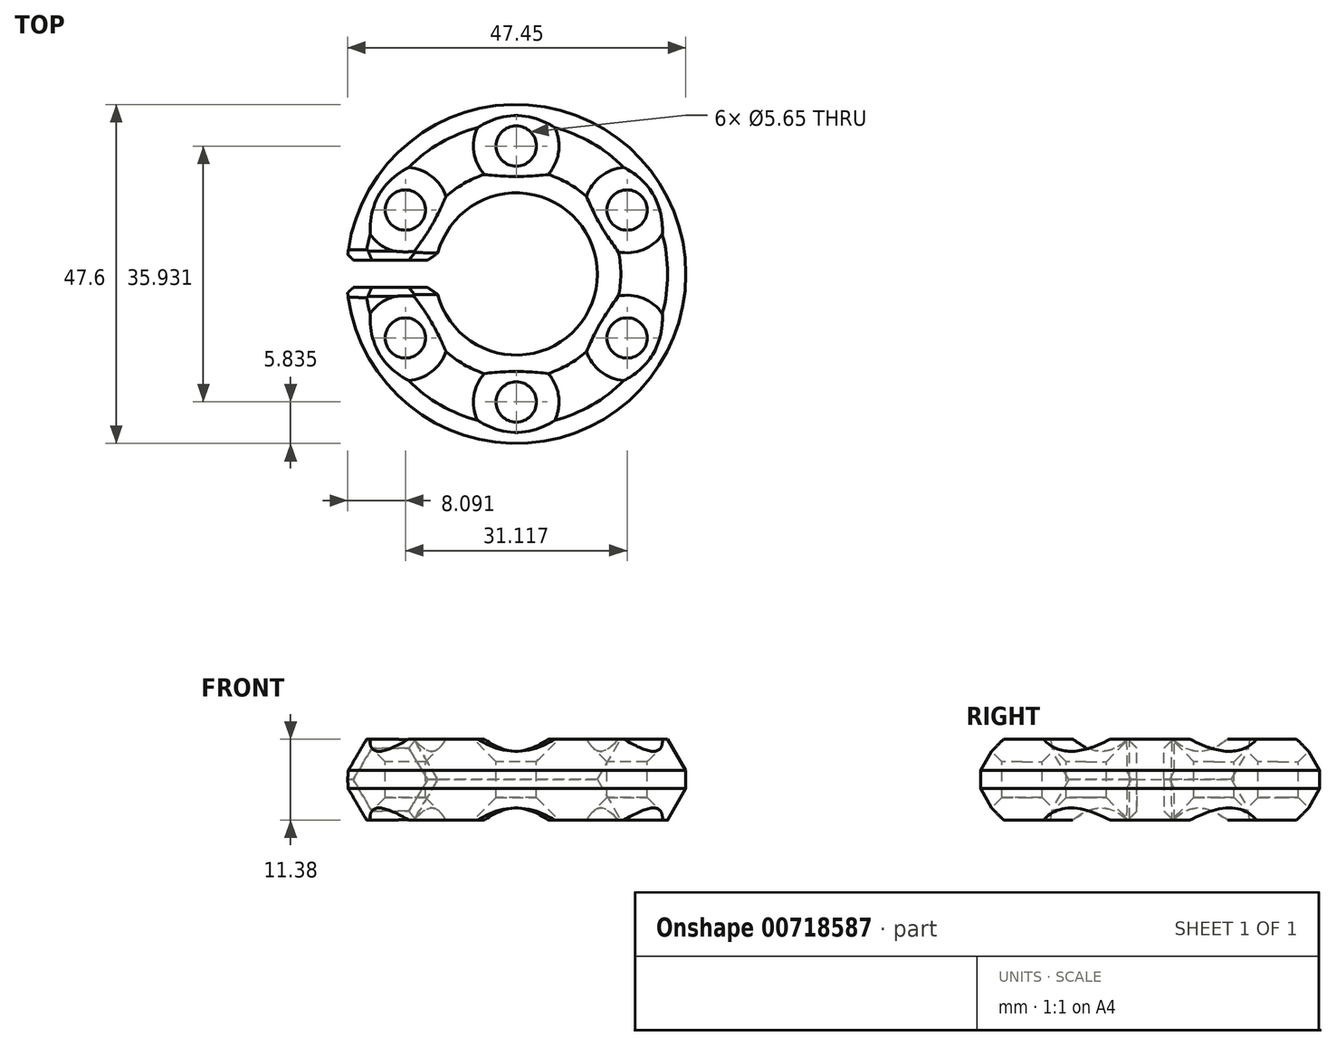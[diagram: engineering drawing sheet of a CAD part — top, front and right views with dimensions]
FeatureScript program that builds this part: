
annotation { "Feature Type Name" : "Feature", "Feature Type Description" : "" }
export const myFeature = defineFeature(function(context is Context, id is Id, definition is map)
    precondition{}
    {
        {
            var Q0;
            Q0=qCreatedBy(makeId("Front.planeOp"),FACE);
            var sketch = newSketch(context, id + "F0", { "sketchPlane" : qUnion([Q0])});
            skCircle(sketch, "E0.cCircle", {"center": v(-17.96, 0) * mm, "radius": 5.7 * mm, "construction": true});
            skLineSegment(sketch, "E0.0", {"start": v(-14.67, -5.7) * mm, "end": v(-21.25, -5.7) * mm});
            skLineSegment(sketch, "E0.1", {"start": v(-21.25, -5.7) * mm, "end": v(-24.53, 0) * mm});
            skLineSegment(sketch, "E0.2", {"start": v(-24.53, 0) * mm, "end": v(-21.25, 5.7) * mm});
            skLineSegment(sketch, "E0.3", {"start": v(-21.25, 5.7) * mm, "end": v(-14.67, 5.7) * mm});
            skLineSegment(sketch, "E0.4", {"start": v(-14.67, 5.7) * mm, "end": v(-11.38, 0) * mm});
            skLineSegment(sketch, "E0.5", {"start": v(-11.38, 0) * mm, "end": v(-14.67, -5.7) * mm});
            skPoint(sketch, "E0.0.midPoint", {"position": v(-17.96, -5.7) * mm});
            skLineSegment(sketch, "E1", {"start": v(0, 30.8) * mm, "end": v(0, -30.51) * mm});
            skSolve(sketch);
        }
        {
            var Q0;
            Q0 = qSketchRegion(id + "F0", true);
            var Q1;
            Q1=sQuery(id+"F0.wireOp",EDGE,"E1");
            revolve(context, id + "F1", {"surfaceOperationType" : NewSurfaceOperationType.NEW, "entities" : qUnion([Q0]), "axis" : qUnion([Q1]), "revolveType" : RevolveType.FULL});
        }
        {
            var Q0;
            Q0=qCreatedBy(makeId("Top.planeOp"),FACE);
            var sketch = newSketch(context, id + "F2", { "sketchPlane" : qUnion([Q0])});
            skLineSegment(sketch, "E2.bottom", {"start": v(-9.68, 1.96) * mm, "end": v(-30.83, 1.96) * mm});
            skLineSegment(sketch, "E2.top", {"start": v(-9.68, -1.87) * mm, "end": v(-30.83, -1.87) * mm});
            skLineSegment(sketch, "E2.left", {"start": v(-9.68, 1.96) * mm, "end": v(-9.68, -1.87) * mm});
            skLineSegment(sketch, "E2.right", {"start": v(-30.83, 1.96) * mm, "end": v(-30.83, -1.87) * mm});
            skSolve(sketch);
        }
        {
            var Q0;
            Q0=makeQuery(id+"F2.imprint","IMPRINT",FACE,{"disambiguationData":[TD([[makeQuery(id+"F2.imprint","IMPRINT",EDGE,{"derivedFrom":sQuery(id+"F2.wireOp",EDGE,"E2.bottom")}),1.0]])]});
            extrude(context, id + "F3", {"entities" : qUnion([Q0]), "operationType" : NewBodyOperationType.REMOVE, "endBound" : BoundingType.SYMMETRIC, "depth" : 18.08 * mm, "offsetDistance" : 25.4 * mm});
        }
        {
            var Q0;
            Q0=makeQuery(id+"F3.boolean.opBoolean","COPY",FACE,{"derivedFrom":makeQuery(id+"F3.opExtrude","SWEPT_FACE",FACE,{"disambiguationData":[OSD([sQuery(id+"F2.wireOp",EDGE,"E2.bottom")])]})});
            var Q1;
            Q1=makeQuery(id+"F3.boolean.opBoolean","COPY",FACE,{"derivedFrom":makeQuery(id+"F3.opExtrude","SWEPT_FACE",FACE,{"disambiguationData":[OSD([sQuery(id+"F2.wireOp",EDGE,"E2.top")])]})});
            chamfer(context, id + "F4", {"entities" : qUnion([Q0, Q1]), "width" : 1.27 * mm, "tangentPropagation" : true});
        }
        {
            var Q0;
            Q0=qCreatedBy(makeId("Top.planeOp"),FACE);
            var sketch = newSketch(context, id + "F5", { "sketchPlane" : qUnion([Q0])});
            skCircle(sketch, "E3", {"center": v(0, -17.97) * mm, "radius": 2.82 * mm});
            skCircle(sketch, "E4.1.0", {"center": v(-15.56, -8.98) * mm, "radius": 2.82 * mm});
            skCircle(sketch, "E4.2.0", {"center": v(-15.56, 8.98) * mm, "radius": 2.82 * mm});
            skCircle(sketch, "E4.3.0", {"center": v(0, 17.97) * mm, "radius": 2.82 * mm});
            skCircle(sketch, "E4.4.0", {"center": v(15.56, 8.98) * mm, "radius": 2.82 * mm});
            skCircle(sketch, "E4.5.0", {"center": v(15.56, -8.98) * mm, "radius": 2.82 * mm});
            skPoint(sketch, "E4.center", {"position": v(0, 0) * mm});
            skLineSegment(sketch, "E4.anchor1", {"start": v(0, 0) * mm, "end": v(0, -17.97) * mm, "construction": true});
            skLineSegment(sketch, "E4.anchor2", {"start": v(0, 0) * mm, "end": v(15.56, -8.98) * mm, "construction": true});
            skSolve(sketch);
        }
        {
            var Q0;
            Q0 = qSketchRegion(id + "F5", true);
            extrude(context, id + "F6", {"entities" : qUnion([Q0]), "operationType" : NewBodyOperationType.REMOVE, "endBound" : BoundingType.SYMMETRIC, "oppositeDirection" : true, "depth" : 25.4 * mm, "offsetDistance" : 25.4 * mm});
        }
        {
            var Q0;
            Q0=makeQuery(id+"F6.boolean.opBoolean","INTERSECT",EDGE,{"derivedFrom":[makeQuery(id+"F1.opRevolve","SWEPT_FACE",FACE,{"disambiguationData":[OSD([sQuery(id+"F0.wireOp",EDGE,"E0.0")])]}),makeQuery(id+"F6.opExtrude","SWEPT_FACE",FACE,{"disambiguationData":[OSD([sQuery(id+"F5.wireOp",EDGE,"E4.1.0")])]})]});
            var Q1;
            Q1=makeQuery(id+"F6.boolean.opBoolean","INTERSECT",EDGE,{"derivedFrom":[makeQuery(id+"F1.opRevolve","SWEPT_FACE",FACE,{"disambiguationData":[OSD([sQuery(id+"F0.wireOp",EDGE,"E0.0")])]}),makeQuery(id+"F6.opExtrude","SWEPT_FACE",FACE,{"disambiguationData":[OSD([sQuery(id+"F5.wireOp",EDGE,"E3")])]})]});
            var Q2;
            Q2=makeQuery(id+"F6.boolean.opBoolean","INTERSECT",EDGE,{"derivedFrom":[makeQuery(id+"F1.opRevolve","SWEPT_FACE",FACE,{"disambiguationData":[OSD([sQuery(id+"F0.wireOp",EDGE,"E0.0")])]}),makeQuery(id+"F6.opExtrude","SWEPT_FACE",FACE,{"disambiguationData":[OSD([sQuery(id+"F5.wireOp",EDGE,"E4.5.0")])]})]});
            var Q3;
            Q3=makeQuery(id+"F6.boolean.opBoolean","INTERSECT",EDGE,{"derivedFrom":[makeQuery(id+"F1.opRevolve","SWEPT_FACE",FACE,{"disambiguationData":[OSD([sQuery(id+"F0.wireOp",EDGE,"E0.0")])]}),makeQuery(id+"F6.opExtrude","SWEPT_FACE",FACE,{"disambiguationData":[OSD([sQuery(id+"F5.wireOp",EDGE,"E4.3.0")])]})]});
            var Q4;
            Q4=makeQuery(id+"F6.boolean.opBoolean","INTERSECT",EDGE,{"derivedFrom":[makeQuery(id+"F1.opRevolve","SWEPT_FACE",FACE,{"disambiguationData":[OSD([sQuery(id+"F0.wireOp",EDGE,"E0.0")])]}),makeQuery(id+"F6.opExtrude","SWEPT_FACE",FACE,{"disambiguationData":[OSD([sQuery(id+"F5.wireOp",EDGE,"E4.2.0")])]})]});
            var Q5;
            Q5=makeQuery(id+"F6.boolean.opBoolean","INTERSECT",EDGE,{"derivedFrom":[makeQuery(id+"F1.opRevolve","SWEPT_FACE",FACE,{"disambiguationData":[OSD([sQuery(id+"F0.wireOp",EDGE,"E0.3")])]}),makeQuery(id+"F6.opExtrude","SWEPT_FACE",FACE,{"disambiguationData":[OSD([sQuery(id+"F5.wireOp",EDGE,"E4.3.0")])]})]});
            var Q6;
            Q6=makeQuery(id+"F6.boolean.opBoolean","INTERSECT",EDGE,{"derivedFrom":[makeQuery(id+"F1.opRevolve","SWEPT_FACE",FACE,{"disambiguationData":[OSD([sQuery(id+"F0.wireOp",EDGE,"E0.3")])]}),makeQuery(id+"F6.opExtrude","SWEPT_FACE",FACE,{"disambiguationData":[OSD([sQuery(id+"F5.wireOp",EDGE,"E4.2.0")])]})]});
            var Q7;
            Q7=makeQuery(id+"F6.boolean.opBoolean","INTERSECT",EDGE,{"derivedFrom":[makeQuery(id+"F1.opRevolve","SWEPT_FACE",FACE,{"disambiguationData":[OSD([sQuery(id+"F0.wireOp",EDGE,"E0.3")])]}),makeQuery(id+"F6.opExtrude","SWEPT_FACE",FACE,{"disambiguationData":[OSD([sQuery(id+"F5.wireOp",EDGE,"E4.5.0")])]})]});
            var Q8;
            Q8=makeQuery(id+"F6.boolean.opBoolean","INTERSECT",EDGE,{"derivedFrom":[makeQuery(id+"F1.opRevolve","SWEPT_FACE",FACE,{"disambiguationData":[OSD([sQuery(id+"F0.wireOp",EDGE,"E0.3")])]}),makeQuery(id+"F6.opExtrude","SWEPT_FACE",FACE,{"disambiguationData":[OSD([sQuery(id+"F5.wireOp",EDGE,"E4.4.0")])]})]});
            var Q9;
            Q9=makeQuery(id+"F6.boolean.opBoolean","INTERSECT",EDGE,{"derivedFrom":[makeQuery(id+"F1.opRevolve","SWEPT_FACE",FACE,{"disambiguationData":[OSD([sQuery(id+"F0.wireOp",EDGE,"E0.3")])]}),makeQuery(id+"F6.opExtrude","SWEPT_FACE",FACE,{"disambiguationData":[OSD([sQuery(id+"F5.wireOp",EDGE,"E4.1.0")])]})]});
            var Q10;
            Q10=makeQuery(id+"F6.boolean.opBoolean","INTERSECT",EDGE,{"derivedFrom":[makeQuery(id+"F1.opRevolve","SWEPT_FACE",FACE,{"disambiguationData":[OSD([sQuery(id+"F0.wireOp",EDGE,"E0.0")])]}),makeQuery(id+"F6.opExtrude","SWEPT_FACE",FACE,{"disambiguationData":[OSD([sQuery(id+"F5.wireOp",EDGE,"E4.4.0")])]})]});
            var Q11;
            Q11=makeQuery(id+"F6.boolean.opBoolean","INTERSECT",EDGE,{"derivedFrom":[makeQuery(id+"F1.opRevolve","SWEPT_FACE",FACE,{"disambiguationData":[OSD([sQuery(id+"F0.wireOp",EDGE,"E0.3")])]}),makeQuery(id+"F6.opExtrude","SWEPT_FACE",FACE,{"disambiguationData":[OSD([sQuery(id+"F5.wireOp",EDGE,"E3")])]})]});
            chamfer(context, id + "F7", {"entities" : qUnion([Q0, Q1, Q2, Q3, Q4, Q5, Q6, Q7, Q8, Q9, Q10, Q11]), "width" : 3.17 * mm, "tangentPropagation" : true});
        }
        {
            var Q0;
            Q0=makeQuery(id+"F1.opRevolve","SWEPT_EDGE",EDGE,{"disambiguationData":[OSD([sQuery(id+"F0.wireOp",EDGE,"E0.1"),sQuery(id+"F0.wireOp",EDGE,"E0.2")])]});
            chamfer(context, id + "F8", {"entities" : qUnion([Q0]), "width" : 2.54 * mm, "tangentPropagation" : true});
        }
    });
